# Revit family: Sanitary_Toilet-Seats_Hansgrohe_60111XXX-GladeLake-S-WC-seat-and-cover-w__888
name_source: partatom
category: Furniture
revit_build: Autodesk Revit 2018 (Build: 20170223_1515(x64)
units: mm (PartAtom-declared; Revit-internal decimal feet)

## family parameters
Always vertical = No
Cut with Voids When Loaded = No
OmniClass Number = 23.31.19.19.17
OmniClass Title = Water Closet Seats
Room Calculation Point = No
Shared = No
Work Plane-Based = Yes

## types (1)
- 450 White
    Always visible = Yes
    BIMobject category = Toilet Seats
    Default Elevation = 1219.2 mm  [stored 4 ft]
    Description = GladeLake S WC seat and cover with top fix
    Design country = Germany
    EAN code = 4059625477601
    Edition number = 1
    GTIN code = https://4059625477601
    IFC Classification = Furnishing Element
    Manufacturer = Hansgrohe
    Manufacturer country = Germany
    Manufacturer name = hansgrohe
    Masterformat 2014 Code = 22 41 13.13
    Masterformat 2014 Description = Residential Water Closets
    Material 1 = Hansgrohe - Plastic - 450 White
    Model = 60111XXX
    OmniClass Code = 23-31 19 19 17
    OmniClass Description = Water Closet Seats
    Product Guid = ffc513d9-e34e-4d5d-95a8-e7ba7432771e
    Product SKU = 60111XXX
    Product data url = https://bimobject.com
    Product family = GladeLake S
    Product group = toilet seats
    Product name = 60111XXX GladeLake S WC seat and cover with top fix
    Product url = https://pro.hansgrohe.com
    QR code = https://bimobject.com
    URL = https://www.hansgrohe.com
    Uniclass 2015 Code = Pr_40_20_93_95
    Uniclass 2015 Name = WC seats and covers
    Uniformat II Code = E2010
    Uniformat II Description = Fixed Furnishings
    Weight Net (Kg) = 2,2

note: [stored X ft] marks values corroborated as IEEE doubles in the binary element streams (Revit-internal decimal feet)

## geometry (parser evidence)
native form markers: Sweep x2
no freeform markers — native parametric forms only
